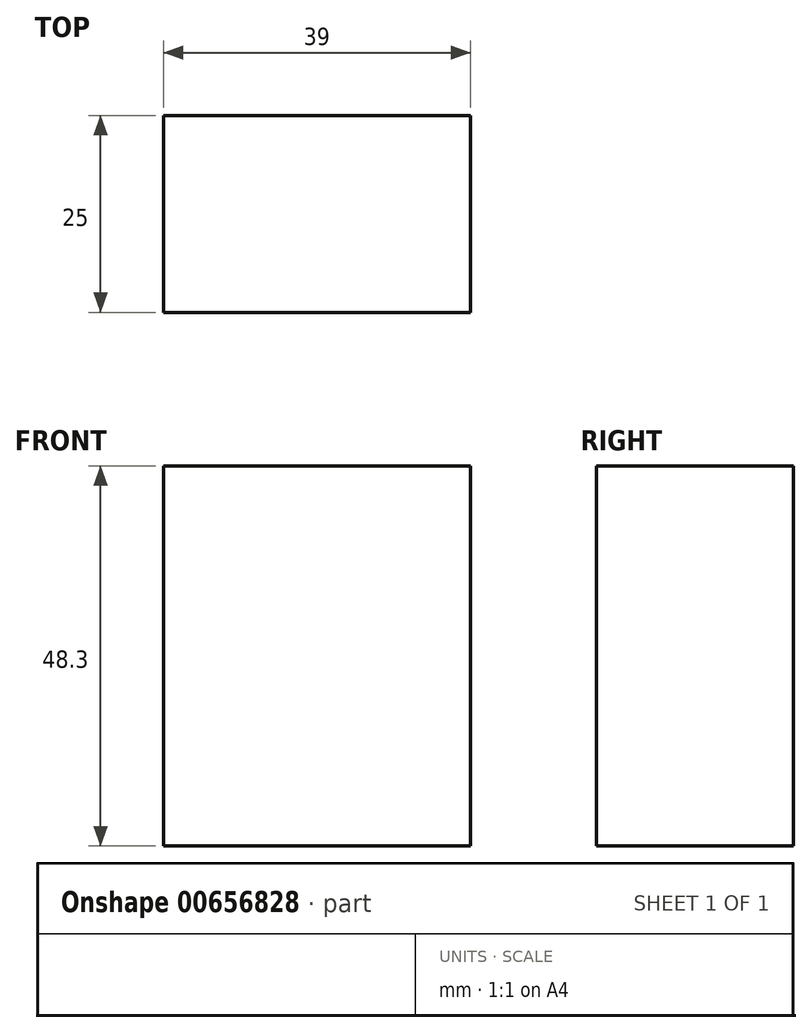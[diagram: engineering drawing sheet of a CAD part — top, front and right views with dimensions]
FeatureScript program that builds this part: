
annotation { "Feature Type Name" : "Feature", "Feature Type Description" : "" }
export const myFeature = defineFeature(function(context is Context, id is Id, definition is map)
    precondition{}
    {
        {
            var Q0;
            Q0=qCreatedBy(makeId("Front.planeOp"),FACE);
            var sketch = newSketch(context, id + "F0", { "sketchPlane" : qUnion([Q0])});
            skLineSegment(sketch, "E0.bottom", {"start": v(-13.05, 22.8) * mm, "end": v(25.95, 22.8) * mm});
            skLineSegment(sketch, "E0.top", {"start": v(-13.05, -25.5) * mm, "end": v(25.95, -25.5) * mm});
            skLineSegment(sketch, "E0.left", {"start": v(-13.05, 22.8) * mm, "end": v(-13.05, -25.5) * mm});
            skLineSegment(sketch, "E0.right", {"start": v(25.95, 22.8) * mm, "end": v(25.95, -25.5) * mm});
            skSolve(sketch);
        }
        {
            var Q0;
            Q0 = qSketchRegion(id + "F0", true);
            extrude(context, id + "F1", {"entities" : qUnion([Q0]), "depth" : 25 * mm, "offsetDistance" : 25 * mm});
        }
    });
